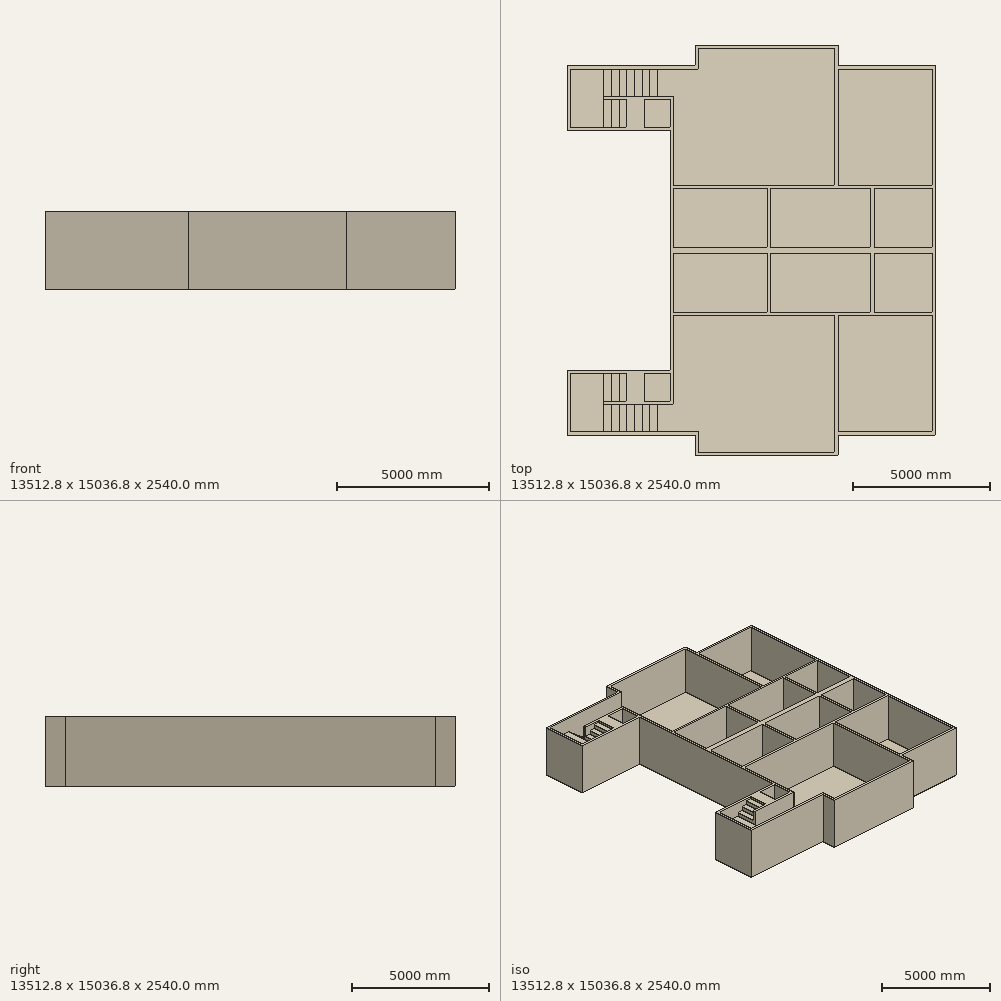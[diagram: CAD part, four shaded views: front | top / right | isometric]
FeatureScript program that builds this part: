
annotation { "Feature Type Name" : "Feature", "Feature Type Description" : "" }
export const myFeature = defineFeature(function(context is Context, id is Id, definition is map)
    precondition{}
    {
        {
            var Q0;
            Q0=qCreatedBy(makeId("Top.planeOp"),FACE);
            var sketch = newSketch(context, id + "F0", { "sketchPlane" : qUnion([Q0])});
            skLineSegment(sketch, "E0", {"start": v(6832.6, 0) * mm, "end": v(16560.8, 0) * mm});
            skLineSegment(sketch, "E1", {"start": v(16560.8, 0) * mm, "end": v(16560.8, 6781.8) * mm});
            skLineSegment(sketch, "E2", {"start": v(16560.8, 6781.8) * mm, "end": v(12979.4, 6781.8) * mm});
            skLineSegment(sketch, "E3", {"start": v(12979.4, 6781.8) * mm, "end": v(12979.4, 7518.4) * mm});
            skLineSegment(sketch, "E4", {"start": v(12979.4, 7518.4) * mm, "end": v(7747, 7518.4) * mm});
            skLineSegment(sketch, "E5", {"start": v(7747, 7518.4) * mm, "end": v(7747, 6781.8) * mm});
            skLineSegment(sketch, "E6", {"start": v(7747, 6781.8) * mm, "end": v(3048, 6781.8) * mm});
            skLineSegment(sketch, "E7", {"start": v(3048, 6781.8) * mm, "end": v(3048, 4394.2) * mm});
            skLineSegment(sketch, "E8", {"start": v(3048, 4394.2) * mm, "end": v(6832.6, 4394.2) * mm});
            skLineSegment(sketch, "E9", {"start": v(6832.6, 4394.2) * mm, "end": v(6832.6, 0) * mm});
            skPoint(sketch, "E10.orphan", {"position": v(0, 0) * mm});
            skSolve(sketch);
        }
        {
            var Q0;
            Q0 = qSketchRegion(id + "F0", true);
            extrude(context, id + "F1", {"entities" : qUnion([Q0]), "depth" : 2540 * mm});
        }
        {
            var Q0;
            Q0=makeQuery(id+"F1.opExtrude","CAP_FACE",FACE,{"disambiguationData":[OSD([sQuery(id+"F0.wireOp",EDGE,"E0"),sQuery(id+"F0.wireOp",EDGE,"E1"),sQuery(id+"F0.wireOp",EDGE,"E2"),sQuery(id+"F0.wireOp",EDGE,"E3"),sQuery(id+"F0.wireOp",EDGE,"E4"),sQuery(id+"F0.wireOp",EDGE,"E5"),sQuery(id+"F0.wireOp",EDGE,"E6"),sQuery(id+"F0.wireOp",EDGE,"E7"),sQuery(id+"F0.wireOp",EDGE,"E8"),sQuery(id+"F0.wireOp",EDGE,"E9")])],"isStart":false});
            var sketch = newSketch(context, id + "F2", { "sketchPlane" : qUnion([Q0])});
            skLineSegment(sketch, "E11.bottom", {"start": v(6959.6, 127) * mm, "end": v(10388.6, 127) * mm});
            skLineSegment(sketch, "E11.top", {"start": v(6959.6, 2260.6) * mm, "end": v(10388.6, 2260.6) * mm});
            skLineSegment(sketch, "E11.left", {"start": v(6959.6, 127) * mm, "end": v(6959.6, 2260.6) * mm});
            skLineSegment(sketch, "E11.right", {"start": v(10388.6, 127) * mm, "end": v(10388.6, 2260.6) * mm});
            skLineSegment(sketch, "E12.bottom", {"start": v(10515.6, 2260.6) * mm, "end": v(14173.2, 2260.6) * mm});
            skLineSegment(sketch, "E12.top", {"start": v(10515.6, 127) * mm, "end": v(14173.2, 127) * mm});
            skLineSegment(sketch, "E12.left", {"start": v(10515.6, 2260.6) * mm, "end": v(10515.6, 127) * mm});
            skLineSegment(sketch, "E12.right", {"start": v(14173.2, 2260.6) * mm, "end": v(14173.2, 127) * mm});
            skLineSegment(sketch, "E13.bottom", {"start": v(14300.2, 2260.6) * mm, "end": v(16433.8, 2260.6) * mm});
            skLineSegment(sketch, "E13.top", {"start": v(14300.2, 127) * mm, "end": v(16433.8, 127) * mm});
            skLineSegment(sketch, "E13.left", {"start": v(14300.2, 2260.6) * mm, "end": v(14300.2, 127) * mm});
            skLineSegment(sketch, "E13.right", {"start": v(16433.8, 2260.6) * mm, "end": v(16433.8, 127) * mm});
            skLineSegment(sketch, "E14.bottom", {"start": v(16433.8, 6654.8) * mm, "end": v(12979.4, 6654.8) * mm});
            skLineSegment(sketch, "E14.top", {"start": v(16433.8, 2387.6) * mm, "end": v(12979.4, 2387.6) * mm});
            skLineSegment(sketch, "E14.left", {"start": v(16433.8, 6654.8) * mm, "end": v(16433.8, 2387.6) * mm});
            skLineSegment(sketch, "E14.right", {"start": v(12979.4, 6654.8) * mm, "end": v(12979.4, 2387.6) * mm});
            skLineSegment(sketch, "E15", {"start": v(6959.6, 2387.6) * mm, "end": v(12852.4, 2387.6) * mm});
            skLineSegment(sketch, "E16", {"start": v(12852.4, 2387.6) * mm, "end": v(12852.4, 7391.4) * mm});
            skLineSegment(sketch, "E17", {"start": v(12852.4, 7391.4) * mm, "end": v(7874, 7391.4) * mm});
            skLineSegment(sketch, "E18", {"start": v(7874, 7391.4) * mm, "end": v(7874, 6654.8) * mm});
            skLineSegment(sketch, "E19", {"start": v(7874, 6654.8) * mm, "end": v(3175, 6654.8) * mm});
            skLineSegment(sketch, "E20", {"start": v(3175, 6654.8) * mm, "end": v(3175, 4521.2) * mm});
            skLineSegment(sketch, "E21", {"start": v(3175, 4521.2) * mm, "end": v(5740.4, 4521.2) * mm});
            skLineSegment(sketch, "E22", {"start": v(6959.6, 5651.5) * mm, "end": v(6959.6, 2387.6) * mm});
            skLineSegment(sketch, "E23", {"start": v(6959.6, 5651.5) * mm, "end": v(4394.2, 5651.5) * mm});
            skLineSegment(sketch, "E24", {"start": v(4394.2, 5651.5) * mm, "end": v(4394.2, 5524.5) * mm});
            skLineSegment(sketch, "E25", {"start": v(4394.2, 5524.5) * mm, "end": v(5740.4, 5524.5) * mm});
            skLineSegment(sketch, "E26", {"start": v(5740.4, 5524.5) * mm, "end": v(5740.4, 4521.2) * mm});
            skLineSegment(sketch, "E27.bottom", {"start": v(5867.4, 4521.2) * mm, "end": v(6832.6, 4521.2) * mm});
            skLineSegment(sketch, "E27.top", {"start": v(5867.4, 5524.5) * mm, "end": v(6832.6, 5524.5) * mm});
            skLineSegment(sketch, "E27.left", {"start": v(5867.4, 4521.2) * mm, "end": v(5867.4, 5524.5) * mm});
            skLineSegment(sketch, "E27.right", {"start": v(6832.6, 4521.2) * mm, "end": v(6832.6, 5524.5) * mm});
            skSolve(sketch);
        }
        {
            var Q0;
            Q0 = qSketchRegion(id + "F2", true);
            extrude(context, id + "F3", {"entities" : qUnion([Q0]), "operationType" : NewBodyOperationType.REMOVE, "oppositeDirection" : true, "depth" : 2336.8 * mm});
        }
        {
            var Q0;
            Q0=makeQuery(id+"F3.boolean.opBoolean","COPY",FACE,{"derivedFrom":makeQuery(id+"F3.opExtrude","SWEPT_FACE",FACE,{"disambiguationData":[OSD([sQuery(id+"F2.wireOp",EDGE,"E25")])]})});
            var sketch = newSketch(context, id + "F4", { "sketchPlane" : qUnion([Q0])});
            skLineSegment(sketch, "E28", {"start": v(5232.4, 2540) * mm, "end": v(5232.4, 2438.4) * mm});
            skLineSegment(sketch, "E29", {"start": v(5232.4, 2438.4) * mm, "end": v(4953, 2438.4) * mm});
            skLineSegment(sketch, "E30", {"start": v(4953, 2438.4) * mm, "end": v(4953, 2235.2) * mm});
            skLineSegment(sketch, "E31", {"start": v(4953, 2235.2) * mm, "end": v(4673.6, 2235.2) * mm});
            skLineSegment(sketch, "E32", {"start": v(4673.6, 2235.2) * mm, "end": v(4673.6, 2032) * mm});
            skLineSegment(sketch, "E33", {"start": v(4673.6, 2032) * mm, "end": v(4394.2, 2032) * mm});
            skLineSegment(sketch, "E34", {"start": v(4394.2, 2032) * mm, "end": v(4394.2, 203.2) * mm});
            skLineSegment(sketch, "E35", {"start": v(4394.2, 203.2) * mm, "end": v(5740.4, 203.2) * mm});
            skLineSegment(sketch, "E36", {"start": v(5740.4, 203.2) * mm, "end": v(5740.4, 2540) * mm});
            skLineSegment(sketch, "E37", {"start": v(5740.4, 2540) * mm, "end": v(5232.4, 2540) * mm});
            skSolve(sketch);
        }
        {
            var Q0;
            Q0 = qSketchRegion(id + "F4", true);
            extrude(context, id + "F5", {"entities" : qUnion([Q0]), "operationType" : NewBodyOperationType.ADD, "depth" : 1003.3 * mm});
        }
        {
            var Q0;
            Q0=makeQuery(id+"F3.boolean.opBoolean","COPY",FACE,{"derivedFrom":makeQuery(id+"F3.opExtrude","SWEPT_FACE",FACE,{"disambiguationData":[OSD([sQuery(id+"F2.wireOp",EDGE,"E21")])]})});
            var sketch = newSketch(context, id + "F6", { "sketchPlane" : qUnion([Q0])});
            skLineSegment(sketch, "E38.bottom", {"start": v(-4394.2, 1828.8) * mm, "end": v(-3175, 1828.8) * mm});
            skLineSegment(sketch, "E38.top", {"start": v(-4394.2, 203.2) * mm, "end": v(-3175, 203.2) * mm});
            skLineSegment(sketch, "E38.left", {"start": v(-4394.2, 1828.8) * mm, "end": v(-4394.2, 203.2) * mm});
            skLineSegment(sketch, "E38.right", {"start": v(-3175, 1828.8) * mm, "end": v(-3175, 203.2) * mm});
            skSolve(sketch);
        }
        {
            var Q0;
            Q0 = qSketchRegion(id + "F6", true);
            extrude(context, id + "F7", {"entities" : qUnion([Q0]), "operationType" : NewBodyOperationType.ADD, "endBound" : BoundingType.UP_TO_NEXT, "depth" : 25.4 * mm});
        }
        {
            var Q0;
            Q0=makeQuery(id+"F3.boolean.opBoolean","COPY",FACE,{"derivedFrom":makeQuery(id+"F3.opExtrude","SWEPT_FACE",FACE,{"disambiguationData":[OSD([sQuery(id+"F2.wireOp",EDGE,"E23")])]})});
            var sketch = newSketch(context, id + "F8", { "sketchPlane" : qUnion([Q0])});
            skLineSegment(sketch, "E39", {"start": v(-4394.2, 203.2) * mm, "end": v(-4394.2, 1625.6) * mm});
            skLineSegment(sketch, "E40", {"start": v(-4394.2, 1625.6) * mm, "end": v(-4673.6, 1625.6) * mm});
            skLineSegment(sketch, "E41", {"start": v(-4673.6, 1625.6) * mm, "end": v(-4673.6, 1422.4) * mm});
            skLineSegment(sketch, "E42", {"start": v(-4673.6, 1422.4) * mm, "end": v(-4953, 1422.4) * mm});
            skLineSegment(sketch, "E43", {"start": v(-4953, 1422.4) * mm, "end": v(-4953, 1219.2) * mm});
            skLineSegment(sketch, "E44", {"start": v(-4953, 1219.2) * mm, "end": v(-5232.4, 1219.2) * mm});
            skLineSegment(sketch, "E45", {"start": v(-5232.4, 1219.2) * mm, "end": v(-5232.4, 1016) * mm});
            skLineSegment(sketch, "E46", {"start": v(-5232.4, 1016) * mm, "end": v(-5511.8, 1016) * mm});
            skLineSegment(sketch, "E47", {"start": v(-5511.8, 1016) * mm, "end": v(-5511.8, 812.8) * mm});
            skLineSegment(sketch, "E48", {"start": v(-5511.8, 812.8) * mm, "end": v(-5791.2, 812.8) * mm});
            skLineSegment(sketch, "E49", {"start": v(-5791.2, 812.8) * mm, "end": v(-5791.2, 609.6) * mm});
            skLineSegment(sketch, "E50", {"start": v(-5791.2, 609.6) * mm, "end": v(-6070.6, 609.6) * mm});
            skLineSegment(sketch, "E51", {"start": v(-6070.6, 609.6) * mm, "end": v(-6070.6, 406.4) * mm});
            skLineSegment(sketch, "E52", {"start": v(-6070.6, 406.4) * mm, "end": v(-6350, 406.4) * mm});
            skLineSegment(sketch, "E53", {"start": v(-6350, 406.4) * mm, "end": v(-6350, 203.2) * mm});
            skLineSegment(sketch, "E54", {"start": v(-6350, 203.2) * mm, "end": v(-4394.2, 203.2) * mm});
            skSolve(sketch);
        }
        {
            var Q0;
            Q0 = qSketchRegion(id + "F8", true);
            extrude(context, id + "F9", {"entities" : qUnion([Q0]), "operationType" : NewBodyOperationType.ADD, "endBound" : BoundingType.UP_TO_NEXT, "depth" : 25.4 * mm});
        }
        {
            var Q0;
            Q0=makeQuery(id+"F1.opExtrude","SWEPT_BODY",BODY,{"disambiguationData":[OSD([sQuery(id+"F0.wireOp",EDGE,"E0"),sQuery(id+"F0.wireOp",EDGE,"E1"),sQuery(id+"F0.wireOp",EDGE,"E2"),sQuery(id+"F0.wireOp",EDGE,"E3"),sQuery(id+"F0.wireOp",EDGE,"E4"),sQuery(id+"F0.wireOp",EDGE,"E5"),sQuery(id+"F0.wireOp",EDGE,"E6"),sQuery(id+"F0.wireOp",EDGE,"E7"),sQuery(id+"F0.wireOp",EDGE,"E8"),sQuery(id+"F0.wireOp",EDGE,"E9")])]});
            var Q1;
            Q1=qCreatedBy(makeId("Front.planeOp"),FACE);
            mirror(context, id + "F10", {"operationType" : NewBodyOperationType.ADD, "entities" : qUnion([Q0]), "mirrorPlane" : qUnion([Q1])});
        }
    });
